# Revit family: oventrop_hydromat-dfc_1064651-55rfa
name_source: partatom
category: Арматура трубопроводов
revit_build: Autodesk Revit 2017 (Build: 20160225_1515(x64)
units: mm (PartAtom-declared; Revit-internal decimal feet)

## family parameters
Всегда вертикально = Да
Заголовок OmniClass = Adjusting/Controlling Valves for Liquid Services
На основе рабочей плоскости = Нет
Номер OmniClass = 23.65.55.14.17
Общий = Нет
При загрузке вырезать с полостями = Нет
Размер круглого соединителя = Использовать радиус
Тип детали = Клапан - Вставляется

## types (5) — shared parameters
Angle = 60.00°
Angle 2 = 30.00°
Angle 3 = -60.00°
Article Description = Differential pressure regulator, flanged
Article Type = Hydromat DFC 10646
Bonnet = Color RGB 35-35-35
Bottom_Flange_Radius = 60.023 мм
Bronze = Color RGB 156-122-90
Cast Iron = Color RGB 140-140-140
Crank Radius = 80 мм
Custom = Нет
EMCS Version = 2.0
ETIM Article Class = EC011463
Family Version = 10.14
Hb4 = 18 мм
Hb5 = 3 мм
Hlp1 = 22 мм
IFCExportAs = IfcValveType
IFCExportType = PRESSUREREDUCING
Lgt1 = 2 мм
MEPcontent Class = VALVE_BALANCING
Manufacturer URL = http://www.oventrop.de
Pressure Drop = 0.0 Па
Product Line = Oventrop
R1 = 9 мм
R2 = 10.392 мм
Revit Version = 2015
Up_Flange_Radius = 103 мм
r1 = 2 мм
r2 = 3 мм
Группа модели = Hydromat DFC 10646
Изготовитель = Oventrop
Описание = Differential pressure regulator, flanged

## per-type parameters (varying)
- DN 65: Body_Height=154 мм; CurDst=23.325 мм; Dst1=28 мм; DstChk=28 мм; FlangeDiameter=185 мм; GTIN=4026755305432; H=191 мм; Hb1=174.36 мм; Hb2=61.035 мм; Hb3=15.259 мм; Hb6=60.308 мм; Height=375 мм; Hlp2=7.775 мм; L2=23.325 мм; Length=290 мм; Lgt2=15.584 мм; Lgt3=34.4 мм; Lgt4=110 мм; Manufacturer Art. No.=1064651; NominalDiameter=65.000 мм; OuterDiameter=76.100 мм; Rad1=69.375 мм; Rad2=92.5 мм; Rad3=43.4 мм; Rad4=40.4 мм; Rad5=42.9 мм; Rad6=32.9 мм; Rad7=44.9 мм; Radius1=32.500 мм; URL=www.stabiplan.com; VDst=29.4 мм; VHth=50.4 мм
- DN 80: Body_Height=160 мм; CurDst=28.001 мм; Dst1=32 мм; DstChk=32 мм; FlangeDiameter=200 мм; GTIN=4026755305449; H=206 мм; Hb1=191.68 мм; Hb2=73.679 мм; Hb3=18.42 мм; Hb6=73.308 мм; Height=395 мм; Hlp2=9.334 мм; L2=28.001 мм; Length=310 мм; Lgt2=16.088 мм; Lgt3=37.1 мм; Lgt4=110 мм; Manufacturer Art. No.=1064652; NominalDiameter=80.000 мм; OuterDiameter=88.900 мм; Rad1=75 мм; Rad2=100 мм; Rad3=51.5 мм; Rad4=48.5 мм; Rad5=51 мм; Rad6=41 мм; Rad7=53 мм; Radius1=40.000 мм; URL=www.stabiplan.com; VDst=32.1 мм; VHth=58.5 мм
- DN 100: Body_Height=134 мм; CurDst=34.237 мм; Dst1=28 мм; DstChk=28 мм; FlangeDiameter=220 мм; GTIN=4026755305456; H=243 мм; Hb1=234.404 мм; Hb2=110.167 мм; Hb3=27.542 мм; Hb6=112.308 мм; Height=410 мм; Hlp2=11.412 мм; L2=34.237 мм; Length=350 мм; Lgt2=16.76 мм; Lgt3=40.7 мм; Lgt4=110 мм; Manufacturer Art. No.=1064653; NominalDiameter=100.000 мм; OuterDiameter=114.300 мм; Rad1=82.5 мм; Rad2=110 мм; Rad3=62.3 мм; Rad4=59.3 мм; Rad5=61.8 мм; Rad6=51.8 мм; Rad7=63.8 мм; Radius1=50.000 мм; URL=www.stabiplan.com; VDst=35.7 мм; VHth=69.3 мм
- DN 125: Body_Height=131 мм; CurDst=42.031 мм; Dst1=25 мм; DstChk=25 мм; FlangeDiameter=250 мм; GTIN=4026755332124; H=286 мм; Hb1=284.056 мм; Hb2=152.025 мм; Hb3=38.006 мм; Hb6=156.808 мм; Height=450 мм; Hlp2=14.01 мм; L2=42.031 мм; Length=400 мм; Lgt2=17.6 мм; Lgt3=45.2 мм; Lgt4=157.5 мм; Manufacturer Art. No.=1064654; NominalDiameter=125.000 мм; OuterDiameter=139.700 мм; Rad1=93.75 мм; Rad2=125 мм; Rad3=75.8 мм; Rad4=72.8 мм; Rad5=75.3 мм; Rad6=65.3 мм; Rad7=77.3 мм; Radius1=62.500 мм; URL=http://file-system.ru; VDst=40.2 мм; VHth=82.8 мм
- DN 150: Body_Height=128 мм; CurDst=49.825 мм; Dst1=40 мм; DstChk=40 мм; FlangeDiameter=285 мм; GTIN=4026755332131; H=288 мм; Hb1=286.366 мм; Hb2=146.54 мм; Hb3=36.635 мм; Hb6=151.308 мм; Height=450 мм; Hlp2=16.608 мм; L2=49.825 мм; Length=480 мм; Lgt2=18.44 мм; Lgt3=49.7 мм; Lgt4=205 мм; Manufacturer Art. No.=1064655; NominalDiameter=150.000 мм; OuterDiameter=168.300 мм; Rad1=106.875 мм; Rad2=142.5 мм; Rad3=89.3 мм; Rad4=86.3 мм; Rad5=88.8 мм; Rad6=78.8 мм; Rad7=90.8 мм; Radius1=75.000 мм; URL=www.stabiplan.com; VDst=44.7 мм; VHth=96.3 мм

## geometry (parser evidence)
native form markers: Blend x2, Sweep x5
no freeform markers — native parametric forms only
